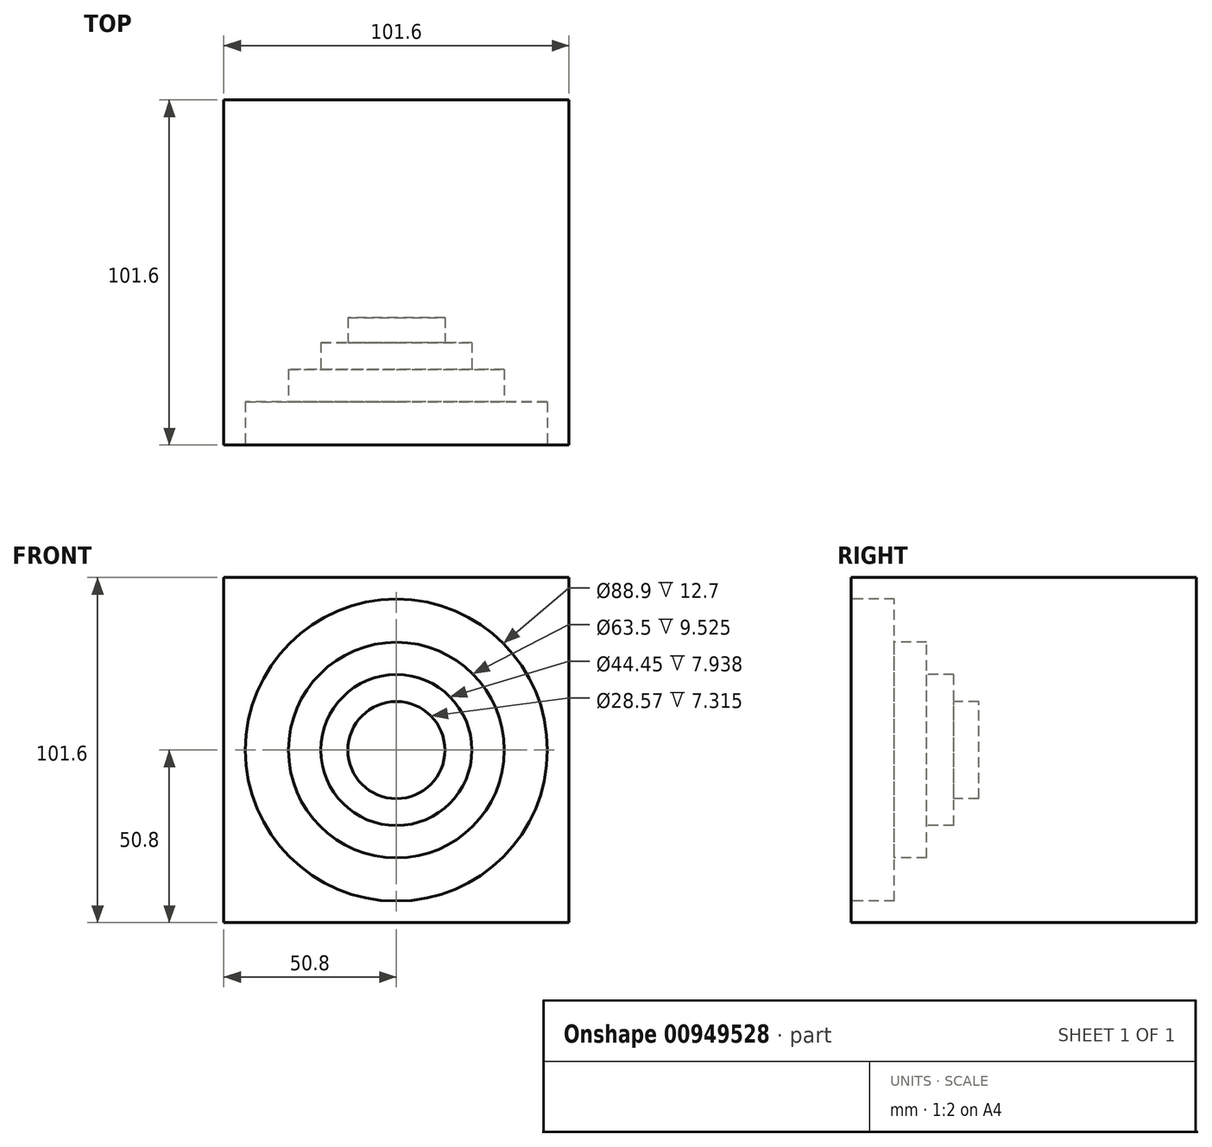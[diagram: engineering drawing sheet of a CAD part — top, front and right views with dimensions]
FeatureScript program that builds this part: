
annotation { "Feature Type Name" : "Feature", "Feature Type Description" : "" }
export const myFeature = defineFeature(function(context is Context, id is Id, definition is map)
    precondition{}
    {
        {
            var Q0;
            Q0=qCreatedBy(makeId("Top.planeOp"),FACE);
            var sketch = newSketch(context, id + "F0", { "sketchPlane" : qUnion([Q0])});
            skLineSegment(sketch, "E0.bottom", {"start": v(50.8, 50.8) * mm, "end": v(-50.8, 50.8) * mm});
            skLineSegment(sketch, "E0.top", {"start": v(50.8, -50.8) * mm, "end": v(-50.8, -50.8) * mm});
            skLineSegment(sketch, "E0.left", {"start": v(50.8, 50.8) * mm, "end": v(50.8, -50.8) * mm});
            skLineSegment(sketch, "E0.right", {"start": v(-50.8, 50.8) * mm, "end": v(-50.8, -50.8) * mm});
            skPoint(sketch, "E0.middle", {"position": v(0, 0) * mm});
            skSolve(sketch);
        }
        {
            var Q0;
            Q0=makeQuery(id+"F0.imprint","IMPRINT",FACE,{"disambiguationData":[TD([[makeQuery(id+"F0.imprint","IMPRINT",EDGE,{"derivedFrom":sQuery(id+"F0.wireOp",EDGE,"E0.bottom")}),1.0]])]});
            extrude(context, id + "F1", {"entities" : qUnion([Q0]), "endBound" : BoundingType.SYMMETRIC, "depth" : 101.6 * mm, "offsetDistance" : 25.4 * mm, "hasSecondDirection" : true, "secondDirectionOppositeDirection" : true, "secondDirectionDepth" : 50.8 * mm});
        }
        {
            var Q0;
            Q0=makeQuery(id+"F1.opExtrude","SWEPT_FACE",FACE,{"disambiguationData":[OSD([sQuery(id+"F0.wireOp",EDGE,"E0.top")])]});
            var sketch = newSketch(context, id + "F2", { "sketchPlane" : qUnion([Q0])});
            skCircle(sketch, "E1", {"center": v(0, 0) * mm, "radius": 44.45 * mm});
            skLineSegment(sketch, "E2", {"start": v(44.45, 50.8) * mm, "end": v(44.45, -50.8) * mm, "construction": true});
            skSolve(sketch);
        }
        {
            var Q0;
            Q0=makeQuery(id+"F2.imprint","IMPRINT",FACE,{"disambiguationData":[TD([[makeQuery(id+"F2.imprint","IMPRINT",EDGE,{"derivedFrom":sQuery(id+"F2.wireOp",EDGE,"E1")}),1.0]])]});
            extrude(context, id + "F3", {"entities" : qUnion([Q0]), "operationType" : NewBodyOperationType.REMOVE, "oppositeDirection" : true, "depth" : 12.7 * mm, "offsetDistance" : 25.4 * mm});
        }
        {
            var Q0;
            Q0=qCreatedBy(makeId("Top.planeOp"),FACE);
            var sketch = newSketch(context, id + "F4", { "sketchPlane" : qUnion([Q0])});
            skLineSegment(sketch, "E3", {"start": v(-90.14, 0) * mm, "end": v(94.98, 0) * mm, "construction": true});
            skSolve(sketch);
        }
        {
            var Q0;
            Q0=qCreatedBy(makeId("Front.planeOp"),FACE);
            var sketch = newSketch(context, id + "F5", { "sketchPlane" : qUnion([Q0])});
            skLineSegment(sketch, "E4", {"start": v(0, 64.25) * mm, "end": v(0, -78.29) * mm, "construction": true});
            skSolve(sketch);
        }
        {
            var Q0;
            Q0=qCreatedBy(makeId("Top.planeOp"),FACE);
            var sketch = newSketch(context, id + "F6", { "sketchPlane" : qUnion([Q0])});
            skLineSegment(sketch, "E5", {"start": v(0, -97.52) * mm, "end": v(0, 91.7) * mm, "construction": true});
            skSolve(sketch);
        }
        {
            var Q0;
            Q0=makeQuery(id+"F3.boolean.opBoolean","COPY",FACE,{"derivedFrom":makeQuery(id+"F3.opExtrude","CAP_FACE",FACE,{"disambiguationData":[OSD([sQuery(id+"F2.wireOp",EDGE,"E1")])],"isStart":false})});
            var sketch = newSketch(context, id + "F7", { "sketchPlane" : qUnion([Q0])});
            skCircle(sketch, "E6", {"center": v(0, 0) * mm, "radius": 31.75 * mm});
            skLineSegment(sketch, "E7", {"start": v(31.75, 38.1) * mm, "end": v(31.75, -38.1) * mm, "construction": true});
            skSolve(sketch);
        }
        {
            var Q0;
            Q0 = qSketchRegion(id + "F7", true);
            extrude(context, id + "F8", {"entities" : qUnion([Q0]), "operationType" : NewBodyOperationType.REMOVE, "oppositeDirection" : true, "depth" : 9.52 * mm, "offsetDistance" : 25.4 * mm});
        }
        {
            var Q0;
            Q0=makeQuery(id+"F8.boolean.opBoolean","COPY",FACE,{"derivedFrom":makeQuery(id+"F8.opExtrude","CAP_FACE",FACE,{"disambiguationData":[OSD([sQuery(id+"F7.wireOp",EDGE,"E6")])],"isStart":false})});
            var sketch = newSketch(context, id + "F9", { "sketchPlane" : qUnion([Q0])});
            skCircle(sketch, "E8", {"center": v(0, 0) * mm, "radius": 22.23 * mm});
            skLineSegment(sketch, "E9", {"start": v(22.23, 28.58) * mm, "end": v(22.23, -28.58) * mm, "construction": true});
            skSolve(sketch);
        }
        {
            var Q0;
            Q0=makeQuery(id+"F9.imprint","IMPRINT",FACE,{"disambiguationData":[TD([[makeQuery(id+"F9.imprint","IMPRINT",EDGE,{"derivedFrom":sQuery(id+"F9.wireOp",EDGE,"E8")}),1.0]])]});
            extrude(context, id + "F10", {"entities" : qUnion([Q0]), "operationType" : NewBodyOperationType.REMOVE, "oppositeDirection" : true, "depth" : 7.94 * mm, "offsetDistance" : 25.4 * mm});
        }
        {
            var Q0;
            Q0=makeQuery(id+"F10.boolean.opBoolean","COPY",FACE,{"derivedFrom":makeQuery(id+"F10.opExtrude","CAP_FACE",FACE,{"disambiguationData":[OSD([sQuery(id+"F9.wireOp",EDGE,"E8")])],"isStart":false})});
            var sketch = newSketch(context, id + "F11", { "sketchPlane" : qUnion([Q0])});
            skCircle(sketch, "E10", {"center": v(0, 0) * mm, "radius": 14.29 * mm});
            skLineSegment(sketch, "E11", {"start": v(14.29, 20.64) * mm, "end": v(14.29, -20.64) * mm, "construction": true});
            skSolve(sketch);
        }
        {
            var Q0;
            Q0=makeQuery(id+"F11.imprint","IMPRINT",FACE,{"disambiguationData":[TD([[makeQuery(id+"F11.imprint","IMPRINT",EDGE,{"derivedFrom":sQuery(id+"F11.wireOp",EDGE,"E10")}),1.0]])]});
            extrude(context, id + "F12", {"entities" : qUnion([Q0]), "operationType" : NewBodyOperationType.REMOVE, "oppositeDirection" : true, "depth" : 7.32 * mm, "offsetDistance" : 25.4 * mm});
        }
        {
            var Q0;
            Q0=makeQuery(id+"F1.opExtrude","CAP_FACE",FACE,{"disambiguationData":[OSD([sQuery(id+"F0.wireOp",EDGE,"E0.bottom"),sQuery(id+"F0.wireOp",EDGE,"E0.top"),sQuery(id+"F0.wireOp",EDGE,"E0.left"),sQuery(id+"F0.wireOp",EDGE,"E0.right")])],"isStart":true});
            var Q1;
            Q1=makeQuery(id+"F1.opExtrude","SWEPT_FACE",FACE,{"disambiguationData":[OSD([sQuery(id+"F0.wireOp",EDGE,"E0.right")])]});
            cPlane(context, id + "F13", {"entities" : qUnion([Q0, Q1]), "cplaneType" : CPlaneType.MID_PLANE, "offset" : 25.4 * mm, "width" : 152.4 * mm, "height" : 152.4 * mm});
        }
        {
            var Q0;
            Q0=qCreatedBy(id+"F13.planeOp",FACE);
            var sketch = newSketch(context, id + "F14", { "sketchPlane" : qUnion([Q0])});
            skLineSegment(sketch, "E12", {"start": v(0, 0) * mm, "end": v(-50.8, -71.84) * mm});
            skSolve(sketch);
        }
        {
            var Q0;
            Q0=sQuery(id+"F14.wireOp",VERTEX,"E12.end");
            var Q1;
            Q1=sQuery(id+"F14.wireOp",EDGE,"E12");
            cPlane(context, id + "F15", {"entities" : qUnion([Q0, Q1]), "cplaneType" : CPlaneType.LINE_POINT, "offset" : 25.4 * mm, "width" : 152.4 * mm, "height" : 152.4 * mm});
        }
        {
            var Q0;
            Q0=qCreatedBy(id+"F15.planeOp",FACE);
            cPlane(context, id + "F16", {"entities" : qUnion([Q0]), "cplaneType" : CPlaneType.OFFSET, "offset" : 12.7 * mm, "oppositeDirection" : true, "width" : 152.4 * mm, "height" : 152.4 * mm});
        }
    });
